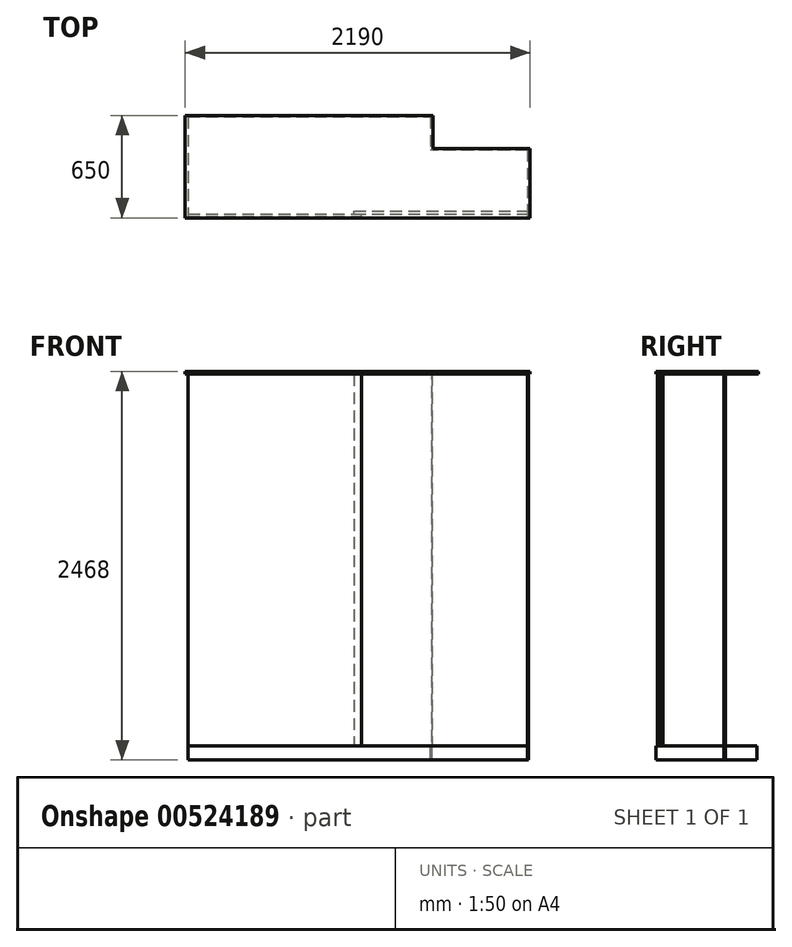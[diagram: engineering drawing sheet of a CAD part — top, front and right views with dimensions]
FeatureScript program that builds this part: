
annotation { "Feature Type Name" : "Feature", "Feature Type Description" : "" }
export const myFeature = defineFeature(function(context is Context, id is Id, definition is map)
    precondition{}
    {
        {
            var Q0;
            Q0=qCreatedBy(makeId("Top.planeOp"),FACE);
            var sketch = newSketch(context, id + "F0", { "sketchPlane" : qUnion([Q0])});
            skLineSegment(sketch, "E0.bottom", {"start": v(0, 0) * mm, "end": v(-2190, 0) * mm});
            skLineSegment(sketch, "E0.top", {"start": v(-615, 650) * mm, "end": v(-2190, 650) * mm});
            skLineSegment(sketch, "E0.left", {"start": v(0, 0) * mm, "end": v(0, 440) * mm});
            skLineSegment(sketch, "E0.right", {"start": v(-2190, 0) * mm, "end": v(-2190, 650) * mm});
            skLineSegment(sketch, "E1.top", {"start": v(-615, 440) * mm, "end": v(0, 440) * mm});
            skLineSegment(sketch, "E1.left", {"start": v(-615, 650) * mm, "end": v(-615, 440) * mm});
            skLineSegment(sketch, "E2.bottom", {"start": v(-2190, 650) * mm, "end": v(-2172, 650) * mm});
            skLineSegment(sketch, "E2.top", {"start": v(-2190, 0) * mm, "end": v(-2172, 0) * mm});
            skLineSegment(sketch, "E2.left", {"start": v(-2190, 650) * mm, "end": v(-2190, 0) * mm});
            skLineSegment(sketch, "E2.right", {"start": v(-2172, 642) * mm, "end": v(-2172, 0) * mm});
            skLineSegment(sketch, "E3.bottom", {"start": v(-615, 650) * mm, "end": v(-624, 650) * mm});
            skLineSegment(sketch, "E3.top", {"start": v(-615, 432) * mm, "end": v(-633, 432) * mm});
            skLineSegment(sketch, "E3.right", {"start": v(-633, 642) * mm, "end": v(-633, 432) * mm});
            skLineSegment(sketch, "E4.bottom", {"start": v(0, 440) * mm, "end": v(-18, 440) * mm});
            skLineSegment(sketch, "E4.top", {"start": v(0, 0) * mm, "end": v(-18, 0) * mm});
            skLineSegment(sketch, "E4.left", {"start": v(0, 440) * mm, "end": v(0, 0) * mm});
            skLineSegment(sketch, "E4.right", {"start": v(-18, 432) * mm, "end": v(-18, 0) * mm});
            skLineSegment(sketch, "E5.bottom", {"start": v(-615, 432) * mm, "end": v(-18, 432) * mm});
            skLineSegment(sketch, "E5.top", {"start": v(-615, 440) * mm, "end": v(-18, 440) * mm});
            skLineSegment(sketch, "E6.bottom", {"start": v(-2172, 650) * mm, "end": v(-633, 650) * mm});
            skLineSegment(sketch, "E6.top", {"start": v(-2172, 642) * mm, "end": v(-633, 642) * mm});
            skLineSegment(sketch, "E7.bottom", {"start": v(-2172, 642) * mm, "end": v(-2180, 642) * mm});
            skLineSegment(sketch, "E7.top", {"start": v(-2171.21, 650) * mm, "end": v(-2180, 650) * mm});
            skLineSegment(sketch, "E7.right", {"start": v(-2180, 642) * mm, "end": v(-2180, 650) * mm});
            skLineSegment(sketch, "E8.bottom", {"start": v(-633, 642) * mm, "end": v(-625, 642) * mm});
            skLineSegment(sketch, "E8.top", {"start": v(-633, 650) * mm, "end": v(-624, 650) * mm});
            skLineSegment(sketch, "E9", {"start": v(-625, 650) * mm, "end": v(-625, 642) * mm});
            skLineSegment(sketch, "E10.trimOffspring", {"start": v(-625, 650) * mm, "end": v(-633, 650) * mm});
            skLineSegment(sketch, "E11.bottom", {"start": v(-615, 440) * mm, "end": v(-623, 440) * mm});
            skLineSegment(sketch, "E11.top", {"start": v(-615, 432) * mm, "end": v(-623, 432) * mm});
            skLineSegment(sketch, "E11.right", {"start": v(-623, 440) * mm, "end": v(-623, 432) * mm});
            skLineSegment(sketch, "E12.bottom", {"start": v(-18, 440) * mm, "end": v(-10, 440) * mm});
            skLineSegment(sketch, "E12.top", {"start": v(-18, 432) * mm, "end": v(-10, 432) * mm});
            skLineSegment(sketch, "E12.right", {"start": v(-10, 440) * mm, "end": v(-10, 432) * mm});
            skLineSegment(sketch, "E13.bottom", {"start": v(-2172, 8) * mm, "end": v(-1072, 8) * mm});
            skLineSegment(sketch, "E13.top", {"start": v(-2172, 26) * mm, "end": v(-1072, 26) * mm});
            skLineSegment(sketch, "E13.left", {"start": v(-2172, 8) * mm, "end": v(-2172, 26) * mm});
            skLineSegment(sketch, "E13.right", {"start": v(-1072, 8) * mm, "end": v(-1072, 26) * mm});
            skLineSegment(sketch, "E14.bottom", {"start": v(-1118, 26) * mm, "end": v(-18, 26) * mm});
            skLineSegment(sketch, "E14.top", {"start": v(-1118, 44) * mm, "end": v(-18, 44) * mm});
            skLineSegment(sketch, "E14.left", {"start": v(-1118, 26) * mm, "end": v(-1118, 44) * mm});
            skLineSegment(sketch, "E14.right", {"start": v(-18, 26) * mm, "end": v(-18, 44) * mm});
            skSolve(sketch);
        }
        {
            var Q0;
            Q0=makeQuery(id+"F0.imprint","IMPRINT",FACE,{"disambiguationData":[TD([[makeQuery(id+"F0.imprint","IMPRINT",EDGE,{"derivedFrom":sQuery(id+"F0.wireOp",EDGE,"E3.bottom")}),1.0]])]});
            var Q1;
            Q1=makeQuery(id+"F0.imprint","IMPRINT",FACE,{"disambiguationData":[TD([[makeQuery(id+"F0.imprint","IMPRINT",EDGE,{"derivedFrom":sQuery(id+"F0.wireOp",EDGE,"E5.bottom")}),1.0]])]});
            var Q2;
            Q2=makeQuery(id+"F0.imprint","IMPRINT",FACE,{"disambiguationData":[TD([[makeQuery(id+"F0.imprint","IMPRINT",EDGE,{"derivedFrom":sQuery(id+"F0.wireOp",EDGE,"E6.bottom")}),-1.0]])]});
            var Q3;
            Q3=makeQuery(id+"F0.imprint","IMPRINT",FACE,{"disambiguationData":[TD([[makeQuery(id+"F0.imprint","IMPRINT",EDGE,{"derivedFrom":sQuery(id+"F0.wireOp",EDGE,"E4.bottom")}),1.0]])]});
            var Q4;
            Q4=makeQuery(id+"F0.imprint","IMPRINT",FACE,{"disambiguationData":[TD([[makeQuery(id+"F0.imprint","IMPRINT",EDGE,{"derivedFrom":sQuery(id+"F0.wireOp",EDGE,"E3.top")}),1.0]])]});
            var Q5;
            Q5=makeQuery(id+"F0.imprint","IMPRINT",FACE,{"disambiguationData":[TD([[makeQuery(id+"F0.imprint","IMPRINT",EDGE,{"derivedFrom":sQuery(id+"F0.wireOp",EDGE,"E14.top")}),-1.0]])]});
            var Q6;
            Q6=makeQuery(id+"F0.imprint","IMPRINT",FACE,{"disambiguationData":[TD([[makeQuery(id+"F0.imprint","IMPRINT",EDGE,{"derivedFrom":sQuery(id+"F0.wireOp",EDGE,"E13.bottom")}),1.0]])]});
            var Q7;
            {var subQ2=sQuery(id+"F0.wireOp",EDGE,"E0.bottom");Q7=makeQuery(id+"F0.imprint","IMPRINT",FACE,{"disambiguationData":[TD([[makeQuery(id+"F0.imprint","IMPRINT",EDGE,{"derivedFrom":subQ2}),-1.0]])]});}
            var Q8;
            Q8=makeQuery(id+"F0.imprint","IMPRINT",FACE,{"disambiguationData":[TD([[makeQuery(id+"F0.imprint","IMPRINT",EDGE,{"derivedFrom":sQuery(id+"F0.wireOp",EDGE,"E2.bottom")}),-1.0]])]});
            extrude(context, id + "F1", {"entities" : qUnion([Q0, Q1, Q2, Q3, Q4, Q5, Q6, Q7, Q8]), "oppositeDirection" : true, "depth" : 90 * mm, "offsetDistance" : 25 * mm});
        }
        {
            var Q0;
            Q0=makeQuery(id+"F0.imprint","IMPRINT",FACE,{"disambiguationData":[TD([[makeQuery(id+"F0.imprint","IMPRINT",EDGE,{"derivedFrom":sQuery(id+"F0.wireOp",EDGE,"E6.bottom")}),-1.0]])]});
            var Q1;
            Q1=makeQuery(id+"F0.imprint","IMPRINT",FACE,{"disambiguationData":[TD([[makeQuery(id+"F0.imprint","IMPRINT",EDGE,{"derivedFrom":sQuery(id+"F0.wireOp",EDGE,"E3.bottom")}),1.0]])]});
            var Q2;
            Q2=makeQuery(id+"F0.imprint","IMPRINT",FACE,{"disambiguationData":[TD([[makeQuery(id+"F0.imprint","IMPRINT",EDGE,{"derivedFrom":sQuery(id+"F0.wireOp",EDGE,"E5.bottom")}),1.0]])]});
            var Q3;
            Q3=makeQuery(id+"F0.imprint","IMPRINT",FACE,{"disambiguationData":[TD([[makeQuery(id+"F0.imprint","IMPRINT",EDGE,{"derivedFrom":sQuery(id+"F0.wireOp",EDGE,"E4.bottom")}),1.0]])]});
            var Q4;
            Q4=makeQuery(id+"F0.imprint","IMPRINT",FACE,{"disambiguationData":[TD([[makeQuery(id+"F0.imprint","IMPRINT",EDGE,{"derivedFrom":sQuery(id+"F0.wireOp",EDGE,"E2.bottom")}),-1.0]])]});
            extrude(context, id + "F2", {"entities" : qUnion([Q0, Q1, Q2, Q3, Q4]), "operationType" : NewBodyOperationType.ADD, "depth" : 2360 * mm, "offsetDistance" : 25 * mm});
        }
        {
            var Q0;
            Q0=makeQuery(id+"F0.imprint","IMPRINT",FACE,{"disambiguationData":[TD([[makeQuery(id+"F0.imprint","IMPRINT",EDGE,{"derivedFrom":sQuery(id+"F0.wireOp",EDGE,"E13.bottom")}),1.0]])]});
            extrude(context, id + "F3", {"entities" : qUnion([Q0]), "depth" : 2360 * mm, "offsetDistance" : 25 * mm});
        }
        {
            var Q0;
            Q0=makeQuery(id+"F0.imprint","IMPRINT",FACE,{"disambiguationData":[TD([[makeQuery(id+"F0.imprint","IMPRINT",EDGE,{"derivedFrom":sQuery(id+"F0.wireOp",EDGE,"E14.top")}),-1.0]])]});
            extrude(context, id + "F4", {"entities" : qUnion([Q0]), "depth" : 2360 * mm, "offsetDistance" : 25 * mm});
        }
        {
            var Q0;
            Q0=makeQuery(id+"F2.opExtrude","CAP_FACE",FACE,{"disambiguationData":[OSD([sQuery(id+"F0.wireOp",EDGE,"E2.bottom"),sQuery(id+"F0.wireOp",EDGE,"E2.top"),sQuery(id+"F0.wireOp",EDGE,"E2.left"),sQuery(id+"F0.wireOp",EDGE,"E2.right"),sQuery(id+"F0.wireOp",EDGE,"E3.bottom"),sQuery(id+"F0.wireOp",EDGE,"E3.top"),sQuery(id+"F0.wireOp",EDGE,"E1.left"),sQuery(id+"F0.wireOp",EDGE,"E3.right"),sQuery(id+"F0.wireOp",EDGE,"E4.bottom"),sQuery(id+"F0.wireOp",EDGE,"E4.top"),sQuery(id+"F0.wireOp",EDGE,"E4.left"),sQuery(id+"F0.wireOp",EDGE,"E4.right"),sQuery(id+"F0.wireOp",EDGE,"E5.bottom"),sQuery(id+"F0.wireOp",EDGE,"E5.top"),sQuery(id+"F0.wireOp",EDGE,"E6.bottom"),sQuery(id+"F0.wireOp",EDGE,"E6.top"),sQuery(id+"F0.wireOp",EDGE,"E7.top"),sQuery(id+"F0.wireOp",EDGE,"E8.top"),sQuery(id+"F0.wireOp",EDGE,"E10.trimOffspring"),sQuery(id+"F0.wireOp",EDGE,"E11.top"),sQuery(id+"F0.wireOp",EDGE,"E12.bottom"),sQuery(id+"F0.wireOp",EDGE,"E13.left"),sQuery(id+"F0.wireOp",EDGE,"E14.right")])],"isStart":false});
            var sketch = newSketch(context, id + "F5", { "sketchPlane" : qUnion([Q0])});
            skLineSegment(sketch, "E15.0.0", {"start": v(-615, 650) * mm, "end": v(-2190, 650) * mm});
            skLineSegment(sketch, "E15.0.1", {"start": v(-2190, 650) * mm, "end": v(-2190, 0) * mm});
            skLineSegment(sketch, "E15.0.2", {"start": v(-2190, 0) * mm, "end": v(-2172, 0) * mm});
            skLineSegment(sketch, "E15.0.3", {"start": v(-2172, 0) * mm, "end": v(-2172, 642) * mm});
            skLineSegment(sketch, "E15.0.4", {"start": v(-2172, 642) * mm, "end": v(-633, 642) * mm});
            skLineSegment(sketch, "E15.0.5", {"start": v(-633, 642) * mm, "end": v(-633, 432) * mm});
            skLineSegment(sketch, "E15.0.6", {"start": v(-633, 432) * mm, "end": v(-18, 432) * mm});
            skLineSegment(sketch, "E15.0.7", {"start": v(-18, 432) * mm, "end": v(-18, 0) * mm});
            skLineSegment(sketch, "E15.0.8", {"start": v(-18, 0) * mm, "end": v(0, 0) * mm});
            skLineSegment(sketch, "E15.0.9", {"start": v(0, 0) * mm, "end": v(0, 440) * mm});
            skLineSegment(sketch, "E15.0.10", {"start": v(0, 440) * mm, "end": v(-615, 440) * mm});
            skLineSegment(sketch, "E15.0.11", {"start": v(-615, 440) * mm, "end": v(-615, 650) * mm});
            skLineSegment(sketch, "E16.bottom", {"start": v(-2190, 650) * mm, "end": v(-615, 650) * mm});
            skLineSegment(sketch, "E16.top", {"start": v(-2190, 0) * mm, "end": v(0, 0) * mm});
            skLineSegment(sketch, "E16.right", {"start": v(0, 440) * mm, "end": v(0, 0) * mm});
            skLineSegment(sketch, "E17.top", {"start": v(-615, 440) * mm, "end": v(0, 440) * mm});
            skLineSegment(sketch, "E17.left", {"start": v(-615, 650) * mm, "end": v(-615, 440) * mm});
            skSolve(sketch);
        }
        {
            var Q0;
            Q0 = qSketchRegion(id + "F5", true);
            extrude(context, id + "F6", {"entities" : qUnion([Q0]), "depth" : 18 * mm, "offsetDistance" : 25 * mm});
        }
    });
